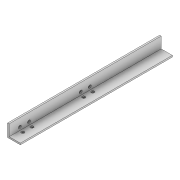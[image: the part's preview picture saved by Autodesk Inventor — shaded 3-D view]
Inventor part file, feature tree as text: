
AUTODESK INVENTOR PART (.ipt)
format: ipt  version: 2022 (Build 260153000, 153)  size: 147,968 bytes
history: native  units: mm
features: extrude x3, sketch x3, mirror x2, projected_geometry x2, other x1, plane x1
ambient origin geometry x8: Origin, YZ Plane, XZ Plane, XY Plane, X Axis, Y Axis, Z Axis, Center Point
bodies: Body1 (feature_tree)
feature tree (12):
  other  "Sólido1"
  extrude  "Extrusión1"  Depth=25.0mm
  extrude  "Extrusión2"  Depth=300.0mm TaperAngle=0.0deg
  plane  "Plano de trabajo1"
  mirror  "Simetría1"
  extrude  "Extrusión3"  Depth=2.0mm
  mirror  "Simetría2"
  sketch  "Boceto1"  dims[d0=25.0mm d1=25.0mm]
  sketch  "Boceto2"  dims[d2=3.0mm d3=300.0mm d4=0.0mm]
  projected_geometry  "Contorno proyectado1"
  sketch  "Boceto3"  dims[d5=3.2mm d6=3.2mm d7=18.0mm d8=9.0mm d9=3.2mm d10=3.2mm d11=18.0mm d12=9.0mm d13=30.0mm d14=9.0mm d15=0.0mm d16=0.0mm d17=6.0mm d18=6.0mm d19=6.0mm d20=6.0mm d21=2.0mm d22=0.0mm]
  projected_geometry  "Contorno proyectado2"
